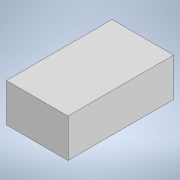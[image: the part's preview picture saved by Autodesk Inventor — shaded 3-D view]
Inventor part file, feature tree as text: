
AUTODESK INVENTOR PART (.ipt)
format: ipt  version: 2020 (Build 240168000, 168)  size: 88,064 bytes
history: native  units: mm
features: extrude x1, sketch x1
ambient origin geometry x8: Origin, YZ Plane, XZ Plane, XY Plane, X Axis, Y Axis, Z Axis, Center Point
bodies: Solid1 (feature_tree)
feature tree (2):
  extrude  "Extrusion1"  Depth=56.0mm
  sketch  "Sketch1"  dims[d0=96.0mm d1=56.0mm d2=28.0mm d3=48.0mm d4=35.0mm d5=0.0mm]
